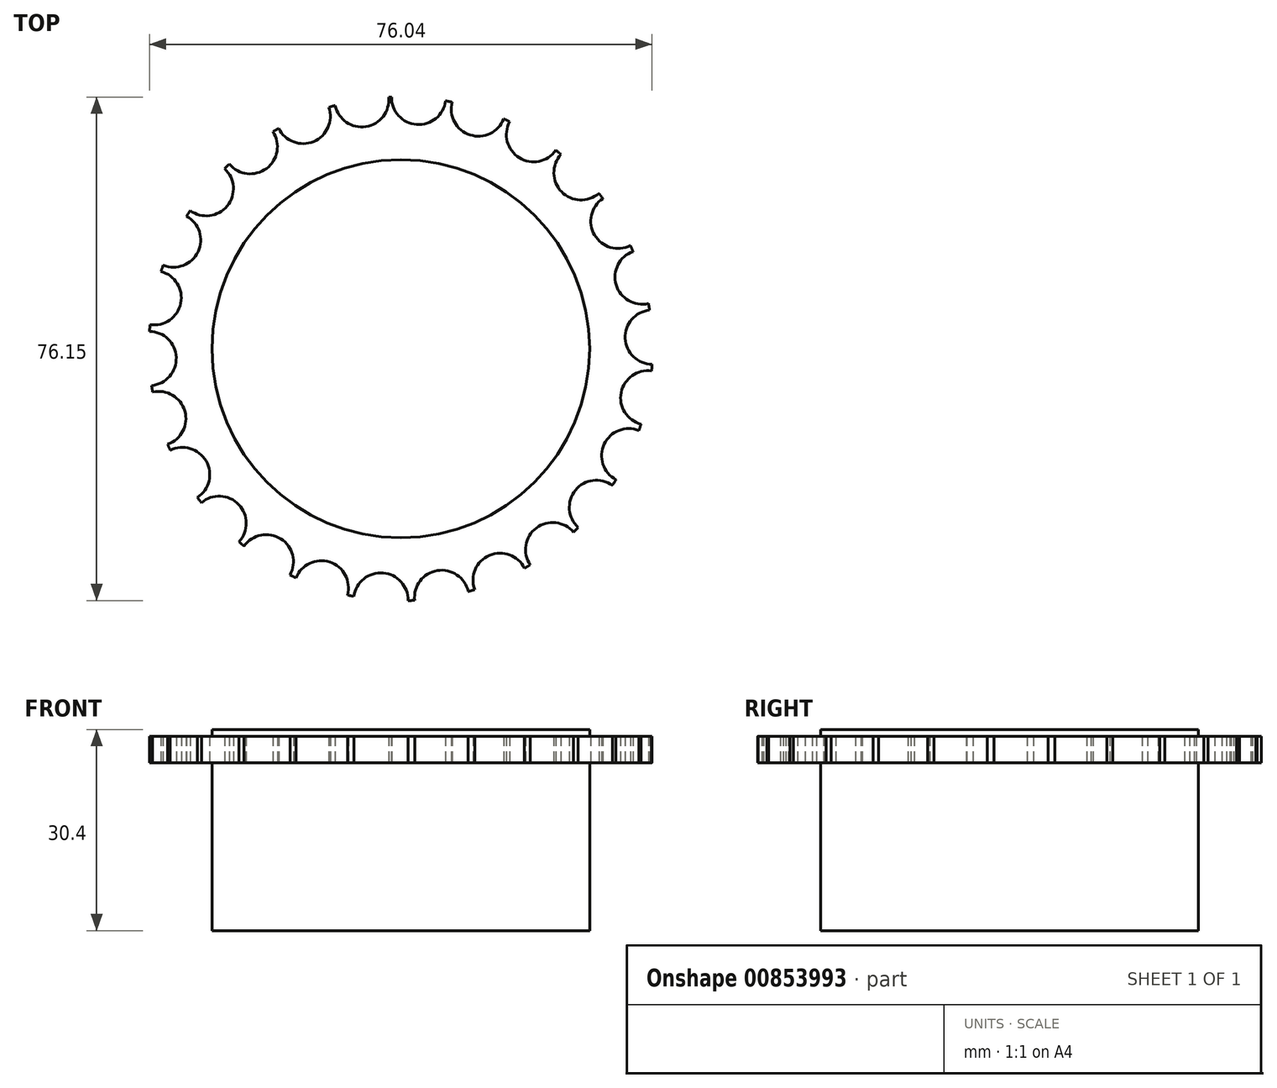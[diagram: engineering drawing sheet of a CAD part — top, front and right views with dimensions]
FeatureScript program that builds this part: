
annotation { "Feature Type Name" : "Feature", "Feature Type Description" : "" }
export const myFeature = defineFeature(function(context is Context, id is Id, definition is map)
    precondition{}
    {
        {
            assignVariable(context, id + "F0", {"name" : "rollerlength", "anyValue" : 4});
        }
        {
            var Q0;
            Q0=qCreatedBy(makeId("Top.planeOp"),FACE);
            var sketch = newSketch(context, id + "F1", { "sketchPlane" : qUnion([Q0])});
            skCircle(sketch, "E0", {"center": v(0, 0) * mm, "radius": 38.1 * mm});
            skCircle(sketch, "E1", {"center": v(-5.91, 37.64) * mm, "radius": 4.1 * mm});
            skCircle(sketch, "E2.1.0", {"center": v(-14.77, 35.12) * mm, "radius": 4.1 * mm});
            skCircle(sketch, "E2.2.0", {"center": v(-22.76, 30.55) * mm, "radius": 4.1 * mm});
            skLineSegment(sketch, "E2.anchor1", {"start": v(0, 0) * mm, "end": v(-5.91, 37.64) * mm, "construction": true});
            skLineSegment(sketch, "E2.anchor2", {"start": v(0, 0) * mm, "end": v(2.7, 38) * mm, "construction": true});
            skCircle(sketch, "E3.1.3.0", {"center": v(-29.43, 24.2) * mm, "radius": 4.1 * mm});
            skCircle(sketch, "E4.1.4.0", {"center": v(-34.37, 16.44) * mm, "radius": 4.1 * mm});
            skCircle(sketch, "E5.1.5.0", {"center": v(-37.31, 7.71) * mm, "radius": 4.1 * mm});
            skCircle(sketch, "E6.1.6.0", {"center": v(-38.07, -1.47) * mm, "radius": 4.1 * mm});
            skCircle(sketch, "E7.1.7.0", {"center": v(-36.6, -10.56) * mm, "radius": 4.1 * mm});
            skCircle(sketch, "E8.1.8.0", {"center": v(-33, -19.03) * mm, "radius": 4.1 * mm});
            skCircle(sketch, "E9.1.9.0", {"center": v(-27.48, -26.4) * mm, "radius": 4.1 * mm});
            skCircle(sketch, "E10.1.10.0", {"center": v(-20.35, -32.21) * mm, "radius": 4.1 * mm});
            skCircle(sketch, "E11.1.11.0", {"center": v(-12.02, -36.15) * mm, "radius": 4.1 * mm});
            skCircle(sketch, "E12.1.12.0", {"center": v(-3, -37.98) * mm, "radius": 4.1 * mm});
            skCircle(sketch, "E13.1.13.0", {"center": v(6.2, -37.6) * mm, "radius": 4.1 * mm});
            skCircle(sketch, "E14.1.14.0", {"center": v(15.04, -35) * mm, "radius": 4.1 * mm});
            skCircle(sketch, "E15.1.15.0", {"center": v(23, -30.38) * mm, "radius": 4.1 * mm});
            skCircle(sketch, "E16.1.16.0", {"center": v(29.61, -23.98) * mm, "radius": 4.1 * mm});
            skCircle(sketch, "E17.1.17.0", {"center": v(34.5, -16.17) * mm, "radius": 4.1 * mm});
            skCircle(sketch, "E18.1.18.0", {"center": v(37.37, -7.42) * mm, "radius": 4.1 * mm});
            skCircle(sketch, "E19.1.19.0", {"center": v(38.06, 1.76) * mm, "radius": 4.1 * mm});
            skCircle(sketch, "E20.1.20.0", {"center": v(36.53, 10.84) * mm, "radius": 4.1 * mm});
            skCircle(sketch, "E21.1.21.0", {"center": v(32.86, 19.28) * mm, "radius": 4.1 * mm});
            skCircle(sketch, "E22.1.22.0", {"center": v(27.28, 26.6) * mm, "radius": 4.1 * mm});
            skCircle(sketch, "E23.1.23.0", {"center": v(20.1, 32.37) * mm, "radius": 4.1 * mm});
            skCircle(sketch, "E24.1.24.0", {"center": v(11.75, 36.24) * mm, "radius": 4.1 * mm});
            skCircle(sketch, "E25.1.25.0", {"center": v(2.7, 38) * mm, "radius": 4.1 * mm});
            skSolve(sketch);
        }
        {
            var Q0;
            {var subQ0=sQuery(id+"F1.wireOp",EDGE,"E0");var subQ42=sQuery(id+"F1.wireOp",EDGE,"E1");var subQ43=makeQuery(id+"F1.imprint","INTERSECT",VERTEX,{"disambiguationData":[OD(0.0)],"derivedFrom":[subQ42,subQ0]});Q0=makeQuery(id+"F1.imprint","IMPRINT",FACE,{"disambiguationData":[TD([[makeQuery(id+"F1.imprint","IMPRINT",EDGE,{"disambiguationData":[TD([[subQ43,1.0]])],"derivedFrom":subQ42}),-1.0]])]});}
            extrude(context, id + "F2", {"entities" : qUnion([Q0]), "depth" : (getVariable(context, 'rollerlength')) * mm, "offsetDistance" : 25.4 * mm});
        }
        {
            var Q0;
            Q0=makeQuery(id+"F2.opExtrude","CAP_FACE",FACE,{"disambiguationData":[OSD([sQuery(id+"F1.wireOp",EDGE,"E1"),sQuery(id+"F1.wireOp",EDGE,"E2.1.0"),sQuery(id+"F1.wireOp",EDGE,"E2.2.0"),sQuery(id+"F1.wireOp",EDGE,"E3.1.3.0"),sQuery(id+"F1.wireOp",EDGE,"E4.1.4.0"),sQuery(id+"F1.wireOp",EDGE,"E5.1.5.0"),sQuery(id+"F1.wireOp",EDGE,"E6.1.6.0"),sQuery(id+"F1.wireOp",EDGE,"E7.1.7.0"),sQuery(id+"F1.wireOp",EDGE,"E8.1.8.0"),sQuery(id+"F1.wireOp",EDGE,"E9.1.9.0"),sQuery(id+"F1.wireOp",EDGE,"E10.1.10.0"),sQuery(id+"F1.wireOp",EDGE,"E11.1.11.0"),sQuery(id+"F1.wireOp",EDGE,"E12.1.12.0"),sQuery(id+"F1.wireOp",EDGE,"E13.1.13.0"),sQuery(id+"F1.wireOp",EDGE,"E14.1.14.0"),sQuery(id+"F1.wireOp",EDGE,"E15.1.15.0"),sQuery(id+"F1.wireOp",EDGE,"E16.1.16.0"),sQuery(id+"F1.wireOp",EDGE,"E17.1.17.0"),sQuery(id+"F1.wireOp",EDGE,"E18.1.18.0"),sQuery(id+"F1.wireOp",EDGE,"E19.1.19.0"),sQuery(id+"F1.wireOp",EDGE,"E20.1.20.0"),sQuery(id+"F1.wireOp",EDGE,"E21.1.21.0"),sQuery(id+"F1.wireOp",EDGE,"E22.1.22.0"),sQuery(id+"F1.wireOp",EDGE,"E23.1.23.0"),sQuery(id+"F1.wireOp",EDGE,"E24.1.24.0"),sQuery(id+"F1.wireOp",EDGE,"E25.1.25.0"),sQuery(id+"F1.wireOp",EDGE,"E0")])],"isStart":true});
            var sketch = newSketch(context, id + "F3", { "sketchPlane" : qUnion([Q0])});
            skCircle(sketch, "E26", {"center": v(0, 0) * mm, "radius": 28.58 * mm});
            skSolve(sketch);
        }
        {
            var Q0;
            Q0 = qSketchRegion(id + "F3", true);
            extrude(context, id + "F4", {"entities" : qUnion([Q0]), "operationType" : NewBodyOperationType.ADD, "depth" : 25.4 * mm, "offsetDistance" : 25.4 * mm, "hasSecondDirection" : true, "secondDirectionOppositeDirection" : true, "secondDirectionDepth" : (getVariable(context, 'rollerlength') + 1) * mm});
        }
    });
